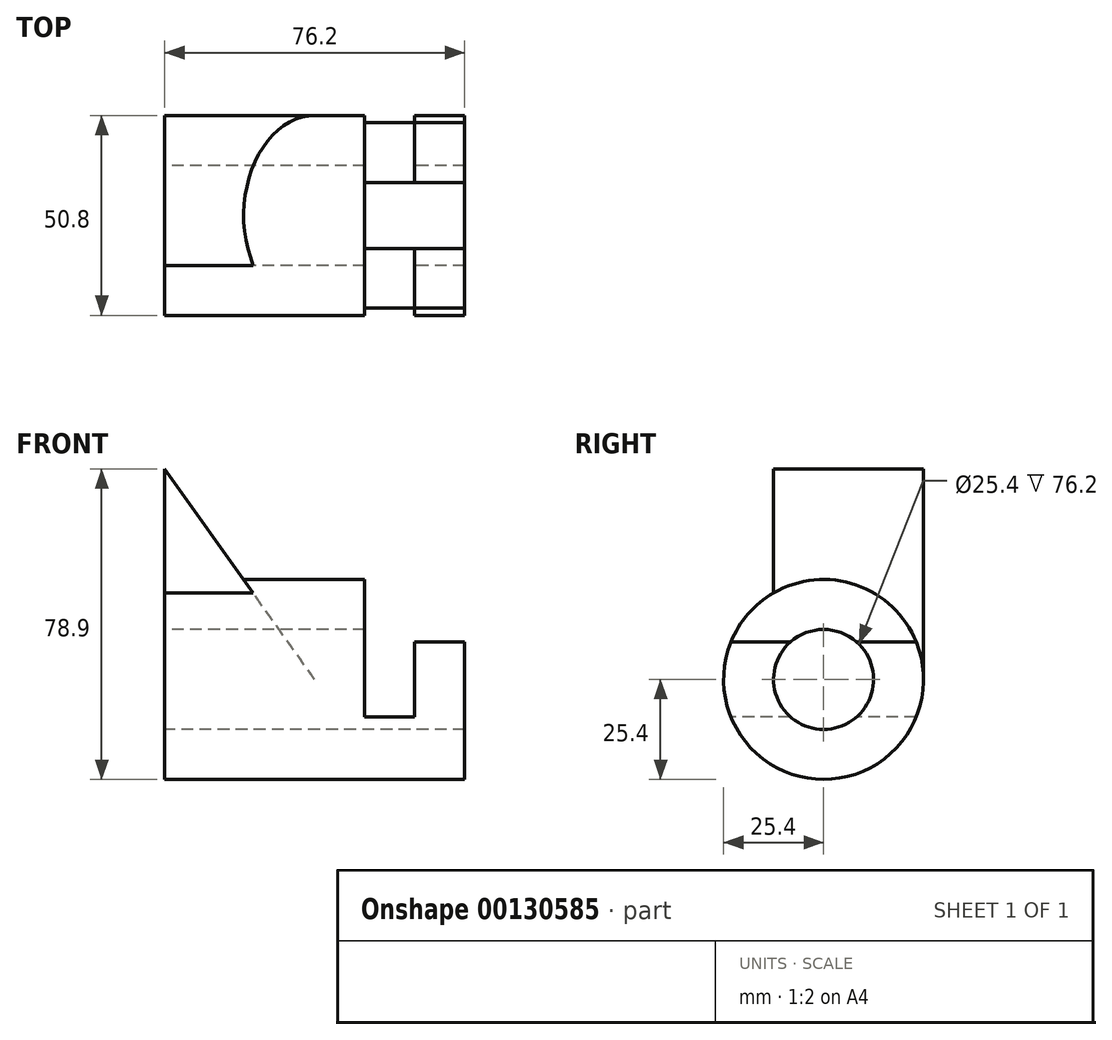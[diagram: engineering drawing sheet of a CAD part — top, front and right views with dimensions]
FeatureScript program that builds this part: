
annotation { "Feature Type Name" : "Feature", "Feature Type Description" : "" }
export const myFeature = defineFeature(function(context is Context, id is Id, definition is map)
    precondition{}
    {
        {
            var Q0;
            Q0=qCreatedBy(makeId("Right.planeOp"),FACE);
            var sketch = newSketch(context, id + "F0", { "sketchPlane" : qUnion([Q0])});
            skCircle(sketch, "E0", {"center": v(0, 0) * mm, "radius": 25.4 * mm});
            skCircle(sketch, "E1", {"center": v(0, 0) * mm, "radius": 12.7 * mm});
            skLineSegment(sketch, "E2", {"start": v(25.4, 0) * mm, "end": v(25.4, 53.5) * mm});
            skLineSegment(sketch, "E3", {"start": v(25.4, 53.5) * mm, "end": v(10.5, 53.5) * mm});
            skLineSegment(sketch, "E4", {"start": v(10.5, 53.5) * mm, "end": v(10.5, 36.78) * mm});
            skLineSegment(sketch, "E5", {"start": v(10.5, 36.78) * mm, "end": v(-19.59, 36.78) * mm});
            skLineSegment(sketch, "E6", {"start": v(-19.59, 36.78) * mm, "end": v(-19.59, 16.17) * mm});
            skSolve(sketch);
        }
        {
            var Q0;
            Q0=makeQuery(id+"F0.imprint","IMPRINT",FACE,{"disambiguationData":[TD([[makeQuery(id+"F0.imprint","IMPRINT",EDGE,{"derivedFrom":sQuery(id+"F0.wireOp",EDGE,"E1")}),-1.0]])]});
            var Q1;
            Q1=sQuery(id+"F0.wireOp",EDGE,"E0");
            extrude(context, id + "F1", {"entities" : qUnion([Q0]), "surfaceEntities" : qUnion([Q1]), "depth" : 76.2 * mm});
        }
        {
            var Q0;
            Q0=qCreatedBy(makeId("Front.planeOp"),FACE);
            var sketch = newSketch(context, id + "F2", { "sketchPlane" : qUnion([Q0])});
            skLineSegment(sketch, "E7", {"start": v(76.2, 25.4) * mm, "end": v(50.8, 25.4) * mm});
            skLineSegment(sketch, "E8", {"start": v(50.8, 25.4) * mm, "end": v(50.8, -9.52) * mm});
            skLineSegment(sketch, "E9", {"start": v(63.5, -9.53) * mm, "end": v(50.8, -9.53) * mm});
            skLineSegment(sketch, "E10", {"start": v(63.5, -9.52) * mm, "end": v(63.5, 9.53) * mm});
            skLineSegment(sketch, "E11", {"start": v(63.5, 9.53) * mm, "end": v(76.2, 9.53) * mm});
            skLineSegment(sketch, "E12", {"start": v(76.2, 9.53) * mm, "end": v(76.2, 25.4) * mm});
            skLineSegment(sketch, "E13", {"start": v(21.6, 25.4) * mm, "end": v(50.8, 25.4) * mm});
            skLineSegment(sketch, "E14", {"start": v(76.2, -25.4) * mm, "end": v(0, -25.4) * mm});
            skSolve(sketch);
        }
        {
            var Q0;
            Q0 = qSketchRegion(id + "F2", true);
            extrude(context, id + "F3", {"entities" : qUnion([Q0]), "operationType" : NewBodyOperationType.REMOVE, "endBound" : BoundingType.THROUGH_ALL, "oppositeDirection" : true, "depth" : 25.4 * mm, "hasSecondDirection" : true, "secondDirectionOppositeDirection" : false, "secondDirectionDepth" : 25.4 * mm});
        }
        {
            var Q0;
            Q0=qCreatedBy(makeId("Front.planeOp"),FACE);
            var sketch = newSketch(context, id + "F4", { "sketchPlane" : qUnion([Q0])});
            skLineSegment(sketch, "E15", {"start": v(0, 53.5) * mm, "end": v(0, 0) * mm});
            skLineSegment(sketch, "E16", {"start": v(0, 0) * mm, "end": v(38.1, 0) * mm});
            skLineSegment(sketch, "E17", {"start": v(38.1, 0) * mm, "end": v(0, 53.5) * mm});
            skSolve(sketch);
        }
        {
            var Q0;
            Q0=makeQuery(id+"F4.imprint","IMPRINT",FACE,{"disambiguationData":[TD([[makeQuery(id+"F4.imprint","IMPRINT",EDGE,{"derivedFrom":sQuery(id+"F4.wireOp",EDGE,"E15")}),1.0]])]});
            extrude(context, id + "F5", {"entities" : qUnion([Q0]), "operationType" : NewBodyOperationType.ADD, "oppositeDirection" : true, "depth" : 25.4 * mm});
        }
        {
            var Q0;
            Q0 = qSketchRegion(id + "F4", true);
            extrude(context, id + "F6", {"entities" : qUnion([Q0]), "operationType" : NewBodyOperationType.ADD, "depth" : 12.7 * mm});
        }
        {
            var Q0;
            Q0=makeQuery(id+"F0.imprint","IMPRINT",FACE,{"disambiguationData":[TD([[makeQuery(id+"F0.imprint","IMPRINT",EDGE,{"derivedFrom":sQuery(id+"F0.wireOp",EDGE,"E1")}),1.0]])]});
            extrude(context, id + "F7", {"entities" : qUnion([Q0]), "operationType" : NewBodyOperationType.REMOVE, "depth" : 50.8 * mm});
        }
    });
